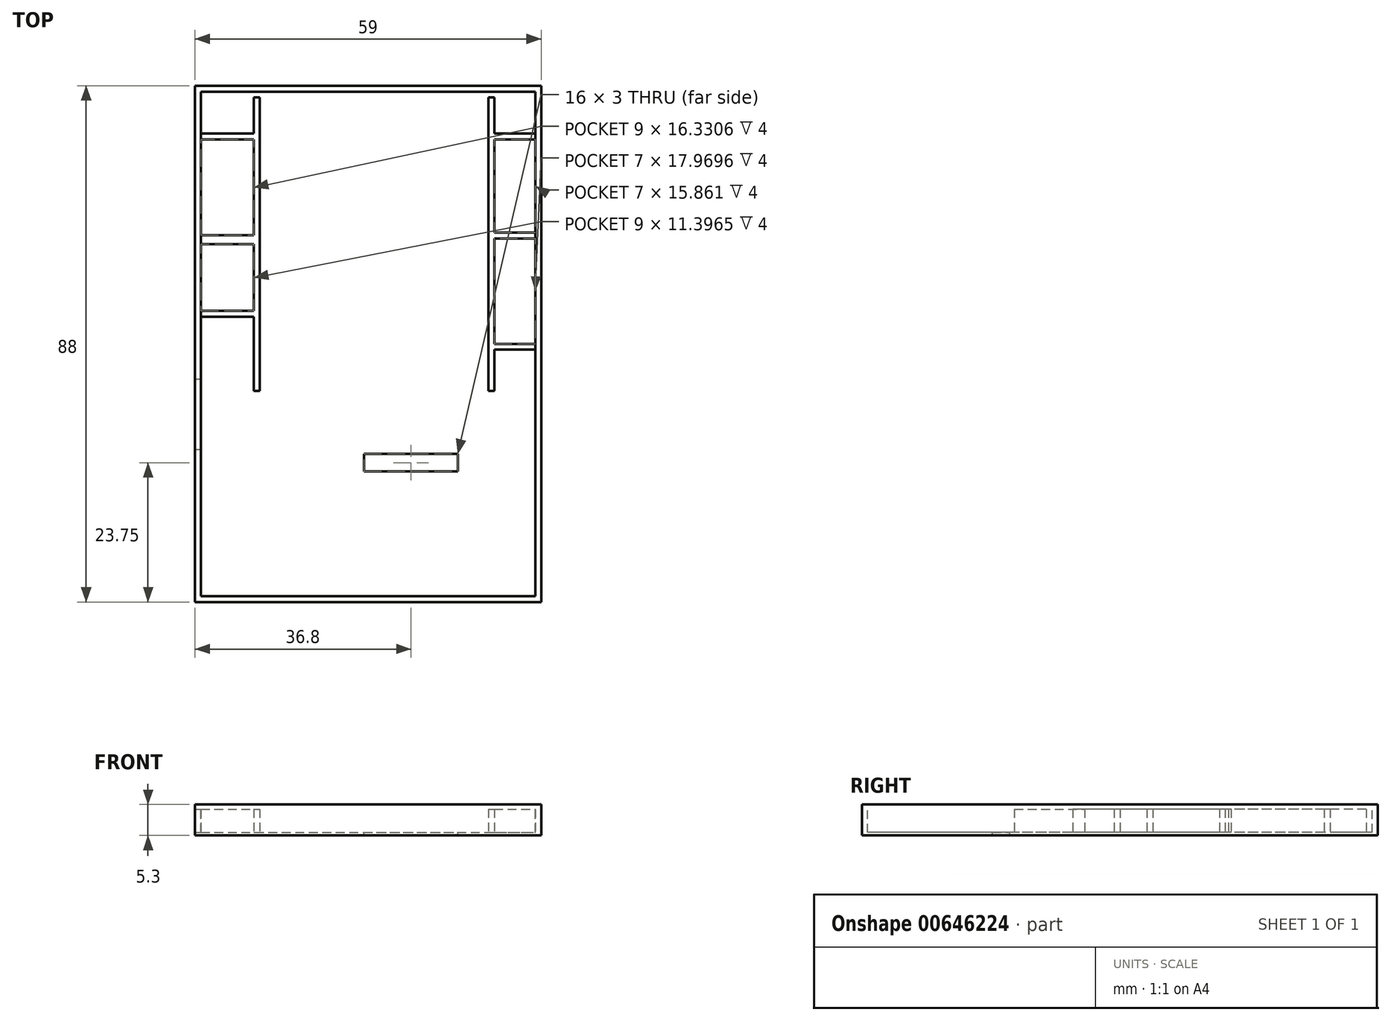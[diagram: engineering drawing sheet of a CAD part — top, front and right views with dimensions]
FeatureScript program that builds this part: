
annotation { "Feature Type Name" : "Feature", "Feature Type Description" : "" }
export const myFeature = defineFeature(function(context is Context, id is Id, definition is map)
    precondition{}
    {
        {
            var Q0;
            Q0=qCreatedBy(makeId("Top.planeOp"),FACE);
            var sketch = newSketch(context, id + "F0", { "sketchPlane" : qUnion([Q0])});
            skLineSegment(sketch, "E0.bottom", {"start": v(-29.5, 44) * mm, "end": v(29.5, 44) * mm});
            skLineSegment(sketch, "E0.top", {"start": v(-29.5, -44) * mm, "end": v(29.5, -44) * mm});
            skLineSegment(sketch, "E0.left", {"start": v(-29.5, 44) * mm, "end": v(-29.5, -44) * mm});
            skLineSegment(sketch, "E0.right", {"start": v(29.5, 44) * mm, "end": v(29.5, -44) * mm});
            skPoint(sketch, "E0.middle", {"position": v(0, 0) * mm});
            skSolve(sketch);
        }
        {
            var Q0;
            Q0=makeQuery(id+"F0.imprint","IMPRINT",FACE,{"disambiguationData":[TD([[makeQuery(id+"F0.imprint","IMPRINT",EDGE,{"derivedFrom":sQuery(id+"F0.wireOp",EDGE,"E0.bottom")}),-1.0]])]});
            extrude(context, id + "F1", {"entities" : qUnion([Q0]), "depth" : 5.3 * mm, "offsetDistance" : 25 * mm});
        }
        {
            var Q0;
            Q0=makeQuery(id+"F1.opExtrude","CAP_FACE",FACE,{"disambiguationData":[OSD([sQuery(id+"F0.wireOp",EDGE,"E0.bottom"),sQuery(id+"F0.wireOp",EDGE,"E0.top"),sQuery(id+"F0.wireOp",EDGE,"E0.left"),sQuery(id+"F0.wireOp",EDGE,"E0.right")])],"isStart":false});
            var sketch = newSketch(context, id + "F2", { "sketchPlane" : qUnion([Q0])});
            skLineSegment(sketch, "E1.bottom", {"start": v(-28.5, 43) * mm, "end": v(28.5, 43) * mm});
            skLineSegment(sketch, "E1.top", {"start": v(-28.5, -43) * mm, "end": v(28.5, -43) * mm});
            skLineSegment(sketch, "E1.left", {"start": v(-28.5, 43) * mm, "end": v(-28.5, -43) * mm});
            skLineSegment(sketch, "E1.right", {"start": v(28.5, 43) * mm, "end": v(28.5, -43) * mm});
            skPoint(sketch, "E1.middle", {"position": v(0, 0) * mm});
            skSolve(sketch);
        }
        {
            var Q0;
            Q0 = qSketchRegion(id + "F2", true);
            var Q1;
            Q1=makeQuery(id+"F2.imprint","IMPRINT",FACE,{"disambiguationData":[TD([[makeQuery(id+"F2.imprint","IMPRINT",EDGE,{"derivedFrom":sQuery(id+"F2.wireOp",EDGE,"E1.bottom")}),-1.0]])]});
            extrude(context, id + "F3", {"entities" : qUnion([Q0, Q1]), "operationType" : NewBodyOperationType.REMOVE, "oppositeDirection" : true, "depth" : 4.8 * mm, "offsetDistance" : 25 * mm});
        }
        {
            var Q0;
            Q0=makeQuery(id+"F3.boolean.opBoolean","COPY",FACE,{"derivedFrom":makeQuery(id+"F3.opExtrude","SWEPT_FACE",FACE,{"disambiguationData":[OSD([sQuery(id+"F2.wireOp",EDGE,"E1.left")])]})});
            var sketch = newSketch(context, id + "F4", { "sketchPlane" : qUnion([Q0])});
            skLineSegment(sketch, "E2.bottom", {"start": v(-18, 4.5) * mm, "end": v(-6, 4.5) * mm});
            skLineSegment(sketch, "E2.top", {"start": v(-18, 0.5) * mm, "end": v(-6, 0.5) * mm});
            skLineSegment(sketch, "E2.left", {"start": v(-18, 4.5) * mm, "end": v(-18, 0.5) * mm});
            skLineSegment(sketch, "E2.right", {"start": v(-6, 4.5) * mm, "end": v(-6, 0.5) * mm});
            skSolve(sketch);
        }
        {
            var Q0;
            Q0=makeQuery(id+"F4.imprint","IMPRINT",FACE,{"disambiguationData":[TD([[makeQuery(id+"F4.imprint","IMPRINT",EDGE,{"derivedFrom":sQuery(id+"F4.wireOp",EDGE,"E2.bottom")}),-1.0]])]});
            extrude(context, id + "F5", {"entities" : qUnion([Q0]), "operationType" : NewBodyOperationType.REMOVE, "oppositeDirection" : true, "depth" : 2 * mm, "offsetDistance" : 25 * mm});
        }
        {
            var Q0;
            Q0=makeQuery(id+"F5.boolean.opBoolean","MERGE",FACE,{"derivedFrom":[makeQuery(id+"F3.boolean.opBoolean","COPY",FACE,{"derivedFrom":makeQuery(id+"F3.opExtrude","CAP_FACE",FACE,{"disambiguationData":[OSD([sQuery(id+"F2.wireOp",EDGE,"E1.bottom"),sQuery(id+"F2.wireOp",EDGE,"E1.top"),sQuery(id+"F2.wireOp",EDGE,"E1.left"),sQuery(id+"F2.wireOp",EDGE,"E1.right")])],"isStart":false})}),makeQuery(id+"F5.opExtrude","SWEPT_FACE",FACE,{"disambiguationData":[OSD([sQuery(id+"F4.wireOp",EDGE,"E2.top")])]})]});
            var sketch = newSketch(context, id + "F6", { "sketchPlane" : qUnion([Q0])});
            skLineSegment(sketch, "E3.bottom", {"start": v(-19.5, 42) * mm, "end": v(-18.5, 42) * mm});
            skLineSegment(sketch, "E3.top", {"start": v(-19.5, -8) * mm, "end": v(-18.5, -8) * mm});
            skLineSegment(sketch, "E3.left", {"start": v(-19.5, 42) * mm, "end": v(-19.5, -8) * mm});
            skLineSegment(sketch, "E3.right", {"start": v(-18.5, 42) * mm, "end": v(-18.5, -8) * mm});
            skLineSegment(sketch, "E4.bottom", {"start": v(20.5, 42) * mm, "end": v(21.5, 42) * mm});
            skLineSegment(sketch, "E4.top", {"start": v(20.5, -8) * mm, "end": v(21.5, -8) * mm});
            skLineSegment(sketch, "E4.left", {"start": v(20.5, 42) * mm, "end": v(20.5, -8) * mm});
            skLineSegment(sketch, "E4.right", {"start": v(21.5, 42) * mm, "end": v(21.5, -8) * mm});
            skSolve(sketch);
        }
        {
            var Q0;
            Q0 = qSketchRegion(id + "F6", true);
            extrude(context, id + "F7", {"entities" : qUnion([Q0]), "operationType" : NewBodyOperationType.ADD, "depth" : 4 * mm, "offsetDistance" : 25 * mm});
        }
        {
            var Q0;
            Q0=makeQuery(id+"F5.boolean.opBoolean","MERGE",FACE,{"derivedFrom":[makeQuery(id+"F3.boolean.opBoolean","COPY",FACE,{"derivedFrom":makeQuery(id+"F3.opExtrude","CAP_FACE",FACE,{"disambiguationData":[OSD([sQuery(id+"F2.wireOp",EDGE,"E1.bottom"),sQuery(id+"F2.wireOp",EDGE,"E1.top"),sQuery(id+"F2.wireOp",EDGE,"E1.left"),sQuery(id+"F2.wireOp",EDGE,"E1.right")])],"isStart":false})}),makeQuery(id+"F5.opExtrude","SWEPT_FACE",FACE,{"disambiguationData":[OSD([sQuery(id+"F4.wireOp",EDGE,"E2.top")])]})]});
            var sketch = newSketch(context, id + "F8", { "sketchPlane" : qUnion([Q0])});
            skLineSegment(sketch, "E5.bottom", {"start": v(-28.5, 35.83) * mm, "end": v(-19.5, 35.83) * mm});
            skLineSegment(sketch, "E5.top", {"start": v(-28.5, 34.83) * mm, "end": v(-19.5, 34.83) * mm});
            skLineSegment(sketch, "E5.left", {"start": v(-28.5, 35.83) * mm, "end": v(-28.5, 34.83) * mm});
            skLineSegment(sketch, "E5.right", {"start": v(-19.5, 35.83) * mm, "end": v(-19.5, 34.83) * mm});
            skLineSegment(sketch, "E6.bottom", {"start": v(-28.5, 5.6) * mm, "end": v(-19.5, 5.6) * mm});
            skLineSegment(sketch, "E6.top", {"start": v(-28.5, 4.6) * mm, "end": v(-19.5, 4.6) * mm});
            skLineSegment(sketch, "E6.left", {"start": v(-28.5, 5.6) * mm, "end": v(-28.5, 4.6) * mm});
            skLineSegment(sketch, "E6.right", {"start": v(-19.5, 5.6) * mm, "end": v(-19.5, 4.6) * mm});
            skLineSegment(sketch, "E7.bottom", {"start": v(21.5, 35.83) * mm, "end": v(28.5, 35.83) * mm});
            skLineSegment(sketch, "E7.top", {"start": v(21.5, 34.83) * mm, "end": v(28.5, 34.83) * mm});
            skLineSegment(sketch, "E7.left", {"start": v(21.5, 35.83) * mm, "end": v(21.5, 34.83) * mm});
            skLineSegment(sketch, "E7.right", {"start": v(28.5, 35.83) * mm, "end": v(28.5, 34.83) * mm});
            skPoint(sketch, "E8.oppositeSnap0", {"position": v(25, 35.83) * mm});
            skLineSegment(sketch, "E9.bottom", {"start": v(21.5, 18.97) * mm, "end": v(28.5, 18.97) * mm});
            skLineSegment(sketch, "E9.top", {"start": v(21.5, 17.97) * mm, "end": v(28.5, 17.97) * mm});
            skLineSegment(sketch, "E9.left", {"start": v(21.5, 18.97) * mm, "end": v(21.5, 17.97) * mm});
            skLineSegment(sketch, "E9.right", {"start": v(28.5, 18.97) * mm, "end": v(28.5, 17.97) * mm});
            skLineSegment(sketch, "E10.bottom", {"start": v(21.5, 0) * mm, "end": v(28.5, 0) * mm});
            skLineSegment(sketch, "E10.top", {"start": v(21.5, -1) * mm, "end": v(28.5, -1) * mm});
            skLineSegment(sketch, "E10.left", {"start": v(21.5, 0) * mm, "end": v(21.5, -1) * mm});
            skLineSegment(sketch, "E10.right", {"start": v(28.5, 0) * mm, "end": v(28.5, -1) * mm});
            skLineSegment(sketch, "E11.bottom", {"start": v(-28.5, 18.5) * mm, "end": v(-19.5, 18.5) * mm});
            skLineSegment(sketch, "E11.top", {"start": v(-28.5, 17) * mm, "end": v(-19.5, 17) * mm});
            skLineSegment(sketch, "E11.left", {"start": v(-28.5, 18.5) * mm, "end": v(-28.5, 17) * mm});
            skLineSegment(sketch, "E11.right", {"start": v(-19.5, 18.5) * mm, "end": v(-19.5, 17) * mm});
            skSolve(sketch);
        }
        {
            var Q0;
            Q0 = qSketchRegion(id + "F8", true);
            extrude(context, id + "F9", {"entities" : qUnion([Q0]), "operationType" : NewBodyOperationType.ADD, "depth" : 4 * mm, "offsetDistance" : 25 * mm});
        }
        {
            var Q0;
            {var subQ0=sQuery(id+"F2.wireOp",EDGE,"E1.right");var subQ1=sQuery(id+"F2.wireOp",EDGE,"E1.bottom");var subQ2=sQuery(id+"F2.wireOp",EDGE,"E1.top");var subQ3=sQuery(id+"F2.wireOp",EDGE,"E1.left");Q0=makeQuery(id+"F9.boolean.opBoolean","SPLIT",FACE,{"disambiguationData":[TD([makeQuery(id+"F1.opExtrude","SWEPT_FACE",FACE,{"disambiguationData":[OSD([sQuery(id+"F0.wireOp",EDGE,"E0.left")])]})])],"derivedFrom":makeQuery(id+"F5.boolean.opBoolean","MERGE",FACE,{"derivedFrom":[makeQuery(id+"F3.boolean.opBoolean","COPY",FACE,{"derivedFrom":makeQuery(id+"F3.opExtrude","CAP_FACE",FACE,{"disambiguationData":[OSD([subQ1,subQ2,subQ3,subQ0])],"isStart":false})}),makeQuery(id+"F5.opExtrude","SWEPT_FACE",FACE,{"disambiguationData":[OSD([sQuery(id+"F4.wireOp",EDGE,"E2.top")])]})]})});}
            var sketch = newSketch(context, id + "F10", { "sketchPlane" : qUnion([Q0])});
            skLineSegment(sketch, "E12.bottom", {"start": v(-0.7, -21.75) * mm, "end": v(15.3, -21.75) * mm});
            skLineSegment(sketch, "E12.top", {"start": v(-0.7, -18.75) * mm, "end": v(15.3, -18.75) * mm});
            skLineSegment(sketch, "E12.left", {"start": v(-0.7, -21.75) * mm, "end": v(-0.7, -18.75) * mm});
            skLineSegment(sketch, "E12.right", {"start": v(15.3, -21.75) * mm, "end": v(15.3, -18.75) * mm});
            skSolve(sketch);
        }
        {
            var Q0;
            Q0 = qSketchRegion(id + "F10", true);
            extrude(context, id + "F11", {"entities" : qUnion([Q0]), "operationType" : NewBodyOperationType.REMOVE, "oppositeDirection" : true, "depth" : 1 * mm, "offsetDistance" : 25 * mm});
        }
    });
